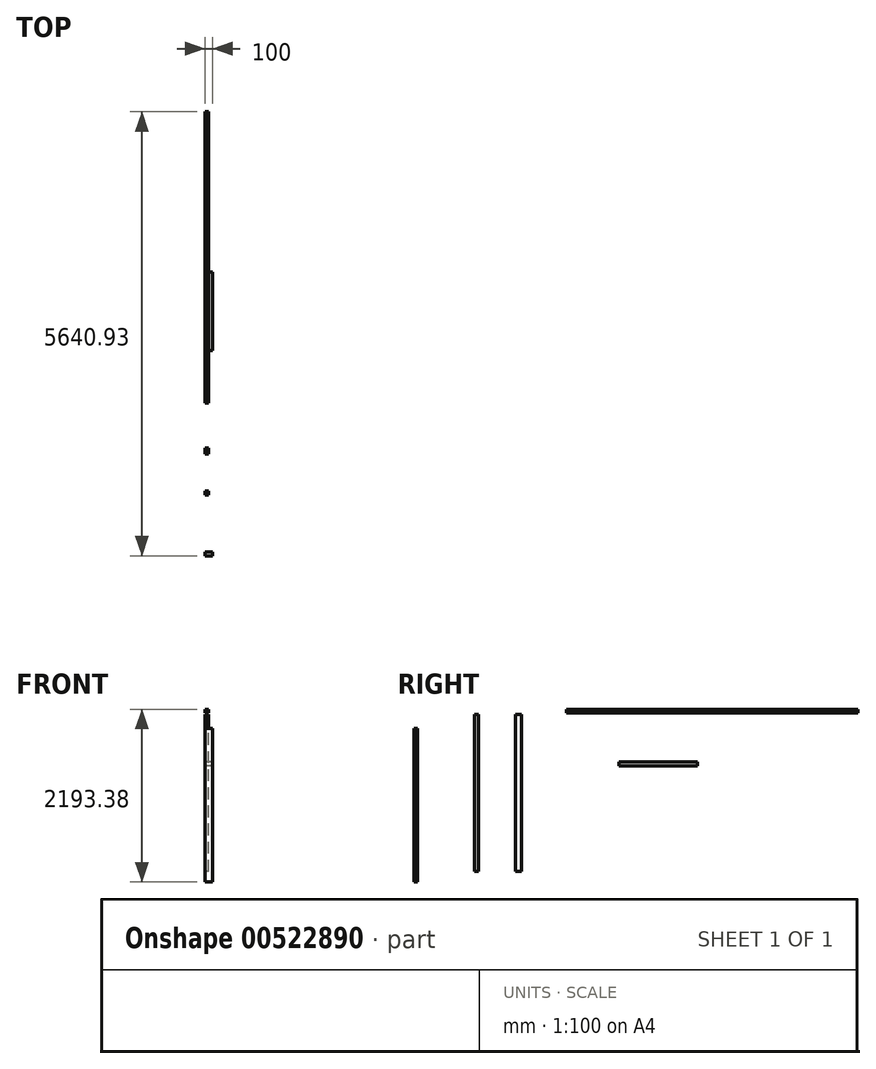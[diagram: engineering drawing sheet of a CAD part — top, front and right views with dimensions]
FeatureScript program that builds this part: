
annotation { "Feature Type Name" : "Feature", "Feature Type Description" : "" }
export const myFeature = defineFeature(function(context is Context, id is Id, definition is map)
    precondition{}
    {
        {
            var Q0;
            Q0=qCreatedBy(makeId("Right.planeOp"),FACE);
            var sketch = newSketch(context, id + "F0", { "sketchPlane" : qUnion([Q0])});
            skLineSegment(sketch, "E0", {"start": v(-397.99, 41.64) * mm, "end": v(3302.01, 41.64) * mm});
            skLineSegment(sketch, "E1", {"start": v(3302.01, 41.64) * mm, "end": v(3302.01, -8.36) * mm});
            skLineSegment(sketch, "E2", {"start": v(3302.01, -8.36) * mm, "end": v(-397.99, -8.36) * mm});
            skLineSegment(sketch, "E3", {"start": v(-397.99, -8.36) * mm, "end": v(-397.99, 41.64) * mm});
            skLineSegment(sketch, "E4", {"start": v(-1046.34, -21.33) * mm, "end": v(-971.34, -21.33) * mm});
            skLineSegment(sketch, "E5", {"start": v(-971.34, -21.33) * mm, "end": v(-971.34, -2021.33) * mm});
            skLineSegment(sketch, "E6", {"start": v(-971.34, -2021.33) * mm, "end": v(-1046.34, -2021.33) * mm});
            skLineSegment(sketch, "E7", {"start": v(-1046.34, -2021.33) * mm, "end": v(-1046.34, -21.33) * mm});
            skLineSegment(sketch, "E8", {"start": v(-1566.99, -21.33) * mm, "end": v(-1516.99, -21.33) * mm});
            skLineSegment(sketch, "E9", {"start": v(-1516.99, -21.33) * mm, "end": v(-1516.99, -2021.33) * mm});
            skLineSegment(sketch, "E10", {"start": v(-1516.99, -2021.33) * mm, "end": v(-1566.99, -2021.33) * mm});
            skLineSegment(sketch, "E11", {"start": v(-1566.99, -2021.33) * mm, "end": v(-1566.99, -21.33) * mm});
            skLineSegment(sketch, "E12", {"start": v(-2288.92, -201.74) * mm, "end": v(-2338.92, -201.74) * mm});
            skLineSegment(sketch, "E13", {"start": v(-2338.92, -201.74) * mm, "end": v(-2338.92, -2151.74) * mm});
            skLineSegment(sketch, "E14", {"start": v(-2338.92, -2151.74) * mm, "end": v(-2288.92, -2151.74) * mm});
            skLineSegment(sketch, "E15", {"start": v(-2288.92, -2151.74) * mm, "end": v(-2288.92, -201.74) * mm});
            skLineSegment(sketch, "E16", {"start": v(1265.43, -629.33) * mm, "end": v(265.43, -629.33) * mm});
            skLineSegment(sketch, "E17", {"start": v(265.43, -629.33) * mm, "end": v(265.43, -679.33) * mm});
            skLineSegment(sketch, "E18", {"start": v(265.43, -679.33) * mm, "end": v(1265.43, -679.33) * mm});
            skLineSegment(sketch, "E19", {"start": v(1265.43, -679.33) * mm, "end": v(1265.43, -629.33) * mm});
            skSolve(sketch);
        }
        {
            var Q0;
            Q0=makeQuery(id+"F0.imprint","IMPRINT",FACE,{"disambiguationData":[TD([[makeQuery(id+"F0.imprint","IMPRINT",EDGE,{"derivedFrom":sQuery(id+"F0.wireOp",EDGE,"E0")}),-1.0]])]});
            var Q1;
            Q1=makeQuery(id+"F0.imprint","IMPRINT",FACE,{"disambiguationData":[TD([[makeQuery(id+"F0.imprint","IMPRINT",EDGE,{"derivedFrom":sQuery(id+"F0.wireOp",EDGE,"E4")}),-1.0]])]});
            var Q2;
            Q2=makeQuery(id+"F0.imprint","IMPRINT",FACE,{"disambiguationData":[TD([[makeQuery(id+"F0.imprint","IMPRINT",EDGE,{"derivedFrom":sQuery(id+"F0.wireOp",EDGE,"E8")}),-1.0]])]});
            extrude(context, id + "F1", {"entities" : qUnion([Q0, Q1, Q2]), "depth" : 50 * mm, "offsetDistance" : 25 * mm});
        }
        {
            var Q0;
            Q0=makeQuery(id+"F0.imprint","IMPRINT",FACE,{"disambiguationData":[TD([[makeQuery(id+"F0.imprint","IMPRINT",EDGE,{"derivedFrom":sQuery(id+"F0.wireOp",EDGE,"E16")}),1.0]])]});
            var Q1;
            Q1=makeQuery(id+"F0.imprint","IMPRINT",FACE,{"disambiguationData":[TD([[makeQuery(id+"F0.imprint","IMPRINT",EDGE,{"derivedFrom":sQuery(id+"F0.wireOp",EDGE,"E12")}),1.0]])]});
            extrude(context, id + "F2", {"entities" : qUnion([Q0, Q1]), "depth" : 100 * mm, "offsetDistance" : 25 * mm});
        }
    });
